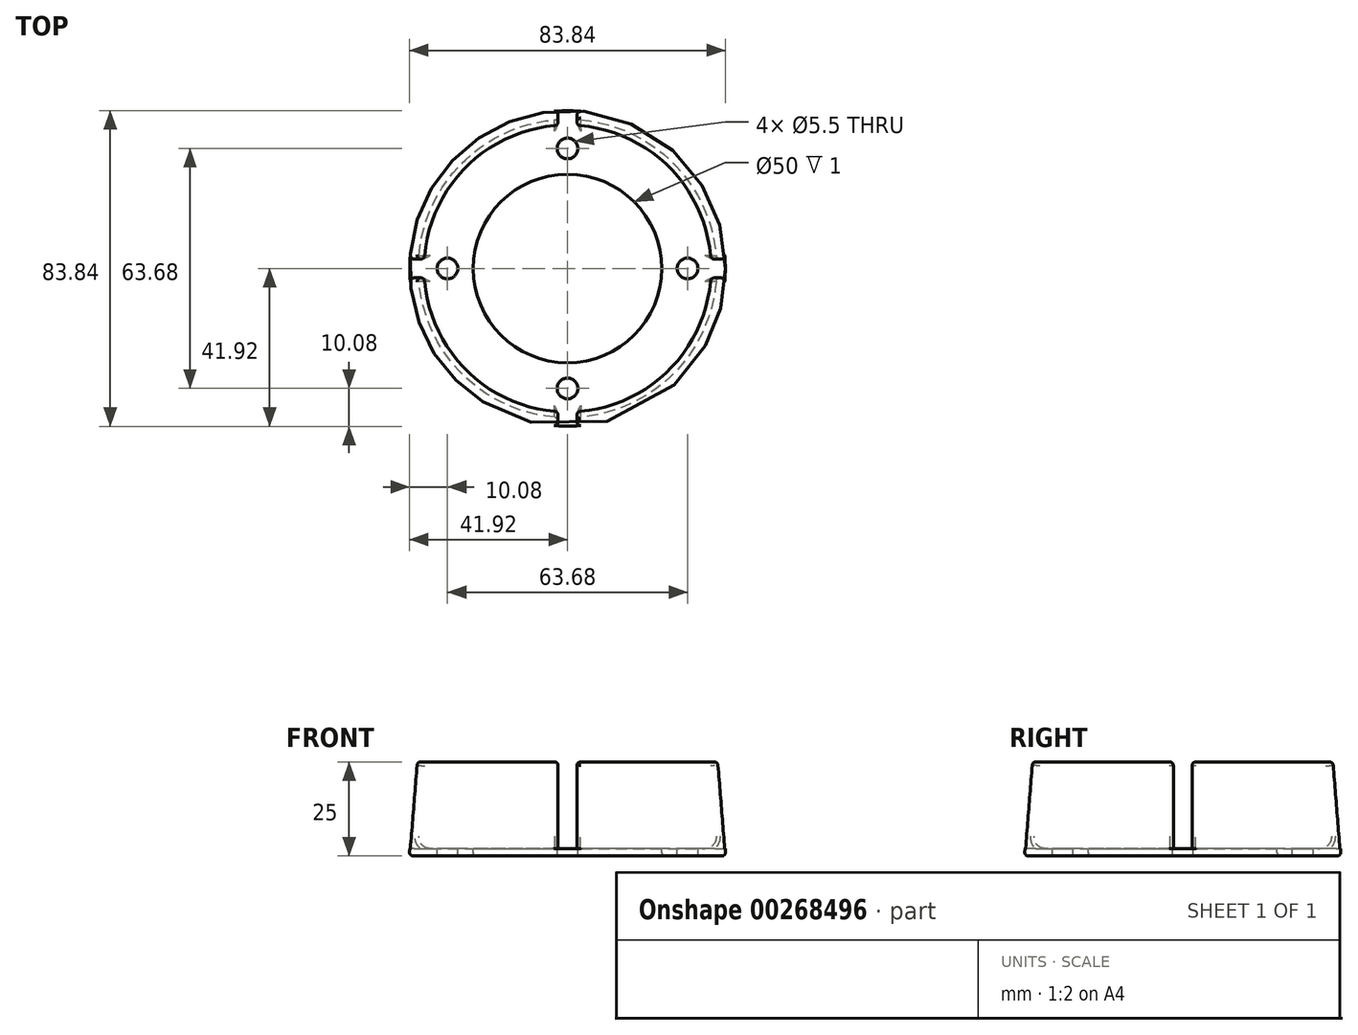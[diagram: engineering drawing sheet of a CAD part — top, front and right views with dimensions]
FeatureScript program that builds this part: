
annotation { "Feature Type Name" : "Feature", "Feature Type Description" : "" }
export const myFeature = defineFeature(function(context is Context, id is Id, definition is map)
    precondition{}
    {
        {
            var Q0;
            Q0=qCreatedBy(makeId("Top.planeOp"),FACE);
            var sketch = newSketch(context, id + "F0", { "sketchPlane" : qUnion([Q0])});
            skCircle(sketch, "E0", {"center": v(0, 0) * mm, "radius": 42 * mm});
            skSolve(sketch);
        }
        {
            var Q0;
            Q0=makeQuery(id+"F0.imprint","IMPRINT",FACE,{"disambiguationData":[TD([[makeQuery(id+"F0.imprint","IMPRINT",EDGE,{"derivedFrom":sQuery(id+"F0.wireOp",EDGE,"E0")}),1.0]])]});
            cPlane(context, id + "F1", {"entities" : qUnion([Q0]), "cplaneType" : CPlaneType.OFFSET, "offset" : 25 * mm, "width" : 150 * mm, "height" : 150 * mm});
        }
        {
            var Q0;
            Q0=qCreatedBy(id+"F1.planeOp",FACE);
            var sketch = newSketch(context, id + "F2", { "sketchPlane" : qUnion([Q0])});
            skCircle(sketch, "E1", {"center": v(0, 0) * mm, "radius": 40 * mm});
            skSolve(sketch);
        }
        {
            var Q0;
            Q0=makeQuery(id+"F0.imprint","IMPRINT",FACE,{"disambiguationData":[TD([[makeQuery(id+"F0.imprint","IMPRINT",EDGE,{"derivedFrom":sQuery(id+"F0.wireOp",EDGE,"E0")}),1.0]])]});
            var Q1;
            Q1=makeQuery(id+"F2.imprint","IMPRINT",FACE,{"disambiguationData":[TD([[makeQuery(id+"F2.imprint","IMPRINT",EDGE,{"derivedFrom":sQuery(id+"F2.wireOp",EDGE,"E1")}),1.0]])]});
            loft(context, id + "F3", {"sheetProfilesArray" : [{ "sheetProfileEntities" : qUnion([Q0]) }, { "sheetProfileEntities" : qUnion([Q1]) }]});
        }
        {
            var Q0;
            Q0=makeQuery(id+"F3.opLoft","CAP_FACE",FACE,{"disambiguationData":[OSD([makeQuery(id+"F2.imprint","IMPRINT",FACE,{"disambiguationData":[TD([[makeQuery(id+"F2.imprint","IMPRINT",EDGE,{"derivedFrom":sQuery(id+"F2.wireOp",EDGE,"E1")}),1.0]])]})])],"isStart":true});
            var Q1;
            Q1=makeQuery(id+"F3.opLoft","SWEPT_BODY",BODY,{"disambiguationData":[OSD([makeQuery(id+"F0.imprint","IMPRINT",FACE,{"disambiguationData":[TD([[makeQuery(id+"F0.imprint","IMPRINT",EDGE,{"derivedFrom":sQuery(id+"F0.wireOp",EDGE,"E0")}),1.0]])]}),makeQuery(id+"F2.imprint","IMPRINT",FACE,{"disambiguationData":[TD([[makeQuery(id+"F2.imprint","IMPRINT",EDGE,{"derivedFrom":sQuery(id+"F2.wireOp",EDGE,"E1")}),1.0]])]})])]});
            shell(context, id + "F4", {"entities" : qUnion([Q0]), "parts" : qUnion([Q1]), "thickness" : 2 * mm});
        }
        {
            var Q0;
            Q0=makeQuery(id+"F4.opShell","OFFSET_FACE",FACE,{"disambiguationData":[OSD([makeQuery(id+"F0.imprint","IMPRINT",FACE,{"disambiguationData":[TD([[makeQuery(id+"F0.imprint","IMPRINT",EDGE,{"derivedFrom":sQuery(id+"F0.wireOp",EDGE,"E0")}),1.0]])]})])]});
            var sketch = newSketch(context, id + "F5", { "sketchPlane" : qUnion([Q0])});
            skCircle(sketch, "E2", {"center": v(0, 0) * mm, "radius": 25 * mm});
            skSolve(sketch);
        }
        {
            var Q0;
            Q0=makeQuery(id+"F5.imprint","IMPRINT",FACE,{"disambiguationData":[TD([[makeQuery(id+"F5.imprint","IMPRINT",EDGE,{"derivedFrom":sQuery(id+"F5.wireOp",EDGE,"E2")}),1.0]])]});
            extrude(context, id + "F6", {"entities" : qUnion([Q0]), "operationType" : NewBodyOperationType.REMOVE, "oppositeDirection" : true, "depth" : 25 * mm});
        }
        {
            var Q0;
            Q0=qCreatedBy(id+"F1.planeOp",FACE);
            var sketch = newSketch(context, id + "F7", { "sketchPlane" : qUnion([Q0])});
            skLineSegment(sketch, "E3.bottom", {"start": v(-2.5, 65.52) * mm, "end": v(2.5, 65.52) * mm});
            skLineSegment(sketch, "E3.top", {"start": v(-2.5, -64.48) * mm, "end": v(2.5, -64.48) * mm});
            skLineSegment(sketch, "E3.left", {"start": v(-2.5, 65.52) * mm, "end": v(-2.5, -64.48) * mm});
            skLineSegment(sketch, "E3.right", {"start": v(2.5, 65.52) * mm, "end": v(2.5, -64.48) * mm});
            skLineSegment(sketch, "E4.bottom", {"start": v(-66.14, 2.5) * mm, "end": v(63.86, 2.5) * mm});
            skLineSegment(sketch, "E4.top", {"start": v(-66.14, -2.5) * mm, "end": v(63.86, -2.5) * mm});
            skLineSegment(sketch, "E4.left", {"start": v(-66.14, 2.5) * mm, "end": v(-66.14, -2.5) * mm});
            skLineSegment(sketch, "E4.right", {"start": v(63.86, 2.5) * mm, "end": v(63.86, -2.5) * mm});
            skSolve(sketch);
        }
        {
            var Q0;
            Q0 = qSketchRegion(id + "F7", true);
            extrude(context, id + "F8", {"entities" : qUnion([Q0]), "operationType" : NewBodyOperationType.REMOVE, "oppositeDirection" : true, "depth" : 23 * mm});
        }
        {
            var Q0;
            Q0=makeQuery(id+"F8.boolean.opBoolean","MERGE",FACE,{"derivedFrom":[makeQuery(id+"F4.opShell","OFFSET_FACE",FACE,{"disambiguationData":[OSD([makeQuery(id+"F0.imprint","IMPRINT",FACE,{"disambiguationData":[TD([[makeQuery(id+"F0.imprint","IMPRINT",EDGE,{"derivedFrom":sQuery(id+"F0.wireOp",EDGE,"E0")}),1.0]])]})])]}),makeQuery(id+"F8.opExtrude","CAP_FACE",FACE,{"disambiguationData":[OSD([sQuery(id+"F7.wireOp",EDGE,"E3.bottom"),sQuery(id+"F7.wireOp",EDGE,"E3.top"),sQuery(id+"F7.wireOp",EDGE,"E3.left"),sQuery(id+"F7.wireOp",EDGE,"E3.right"),sQuery(id+"F7.wireOp",EDGE,"E4.bottom"),sQuery(id+"F7.wireOp",EDGE,"E4.top"),sQuery(id+"F7.wireOp",EDGE,"E4.left"),sQuery(id+"F7.wireOp",EDGE,"E4.right")])],"isStart":false})]});
            var sketch = newSketch(context, id + "F9", { "sketchPlane" : qUnion([Q0])});
            skPoint(sketch, "E5", {"position": v(0, 31.84) * mm});
            skPoint(sketch, "E6.MirrorP", {"position": v(0, -31.84) * mm});
            skPoint(sketch, "E7", {"position": v(31.84, 0) * mm});
            skPoint(sketch, "E8.MirrorP", {"position": v(-31.84, 0) * mm});
            skSolve(sketch);
        }
        {
            var Q0;
            Q0=sQuery(id+"F9.wireOp",VERTEX,"E5");
            var Q1;
            Q1=sQuery(id+"F9.wireOp",VERTEX,"E8.MirrorP");
            var Q2;
            Q2=sQuery(id+"F9.wireOp",VERTEX,"E6.MirrorP");
            var Q3;
            Q3=sQuery(id+"F9.wireOp",VERTEX,"E7");
            var Q4;
            Q4=makeQuery(id+"F3.opLoft","SWEPT_BODY",BODY,{"disambiguationData":[OSD([makeQuery(id+"F0.imprint","IMPRINT",FACE,{"disambiguationData":[TD([[makeQuery(id+"F0.imprint","IMPRINT",EDGE,{"derivedFrom":sQuery(id+"F0.wireOp",EDGE,"E0")}),1.0]])]}),makeQuery(id+"F2.imprint","IMPRINT",FACE,{"disambiguationData":[TD([[makeQuery(id+"F2.imprint","IMPRINT",EDGE,{"derivedFrom":sQuery(id+"F2.wireOp",EDGE,"E1")}),1.0]])]})])]});
            hole(context, id + "F10", {"style" : HoleStyle.SIMPLE, "endStyle" : HoleEndStyle.BLIND, "standardTappedOrClearance" : lookupTablePath({ "standard" : "ISO", "fit" : "Normal", "size" : "M5", "type" : "Clearance" }), "standardBlindInLast" : lookupTablePath({ "fit" : "Standard", "standard" : "ISO", "size" : "M5", "type" : "Clearance" }), "holeDiameter" : 5.5 * mm, "holeDepth" : 50 * mm, "tappedDepth" : 12 * mm, "tapClearance" : 3, "locations" : qUnion([Q0, Q1, Q2, Q3]), "scope" : qUnion([Q4])});
        }
        {
            var Q0;
            {var subQ2=sQuery(id+"F7.wireOp",EDGE,"E3.left");var subQ3=sQuery(id+"F7.wireOp",EDGE,"E3.bottom");var subQ5=sQuery(id+"F0.wireOp",EDGE,"E0");Q0=makeQuery(id+"F8.boolean.opBoolean","SPLIT",EDGE,{"disambiguationData":[TD([makeQuery(id+"F8.opExtrude","SWEPT_FACE",FACE,{"disambiguationData":[OSD([subQ2]),TDD([makeQuery(id+"F7.imprint","IMPRINT",EDGE,{"disambiguationData":[TD([[makeQuery(id+"F7.imprint","INTERSECT",VERTEX,{"derivedFrom":[subQ3,subQ2]}),-1.0]])],"derivedFrom":subQ2})])]})])],"derivedFrom":makeQuery(id+"F4.opShell","OFFSET_EDGE",EDGE,{"disambiguationData":[OSD([subQ5])]})});}
            var Q1;
            {var subQ0=sQuery(id+"F7.wireOp",EDGE,"E3.right");var subQ1=sQuery(id+"F7.wireOp",EDGE,"E3.bottom");var subQ4=sQuery(id+"F0.wireOp",EDGE,"E0");Q1=makeQuery(id+"F8.boolean.opBoolean","SPLIT",EDGE,{"disambiguationData":[TD([makeQuery(id+"F8.opExtrude","SWEPT_FACE",FACE,{"disambiguationData":[OSD([subQ0]),TDD([makeQuery(id+"F7.imprint","IMPRINT",EDGE,{"disambiguationData":[TD([[makeQuery(id+"F7.imprint","INTERSECT",VERTEX,{"derivedFrom":[subQ1,subQ0]}),-1.0]])],"derivedFrom":subQ0})])]})])],"derivedFrom":makeQuery(id+"F4.opShell","OFFSET_EDGE",EDGE,{"disambiguationData":[OSD([subQ4])]})});}
            var Q2;
            {var subQ0=sQuery(id+"F7.wireOp",EDGE,"E3.left");var subQ1=sQuery(id+"F7.wireOp",EDGE,"E3.top");var subQ5=sQuery(id+"F0.wireOp",EDGE,"E0");Q2=makeQuery(id+"F8.boolean.opBoolean","SPLIT",EDGE,{"disambiguationData":[TD([makeQuery(id+"F8.opExtrude","SWEPT_FACE",FACE,{"disambiguationData":[OSD([subQ0]),TDD([makeQuery(id+"F7.imprint","IMPRINT",EDGE,{"disambiguationData":[TD([[makeQuery(id+"F7.imprint","INTERSECT",VERTEX,{"derivedFrom":[subQ1,subQ0]}),1.0]])],"derivedFrom":subQ0})])]})])],"derivedFrom":makeQuery(id+"F4.opShell","OFFSET_EDGE",EDGE,{"disambiguationData":[OSD([subQ5])]})});}
            var Q3;
            {var subQ0=sQuery(id+"F7.wireOp",EDGE,"E3.right");var subQ1=sQuery(id+"F7.wireOp",EDGE,"E3.top");var subQ5=sQuery(id+"F0.wireOp",EDGE,"E0");Q3=makeQuery(id+"F8.boolean.opBoolean","SPLIT",EDGE,{"disambiguationData":[TD([makeQuery(id+"F8.opExtrude","SWEPT_FACE",FACE,{"disambiguationData":[OSD([subQ0]),TDD([makeQuery(id+"F7.imprint","IMPRINT",EDGE,{"disambiguationData":[TD([[makeQuery(id+"F7.imprint","INTERSECT",VERTEX,{"derivedFrom":[subQ1,subQ0]}),1.0]])],"derivedFrom":subQ0})])]})])],"derivedFrom":makeQuery(id+"F4.opShell","OFFSET_EDGE",EDGE,{"disambiguationData":[OSD([subQ5])]})});}
            fillet(context, id + "F11", {"entities" : qUnion([Q0, Q1, Q2, Q3]), "radius" : 3 * mm, "tangentPropagation" : true, "allowEdgeOverflow" : false});
        }
        {
            var Q0;
            {var subQ0=sQuery(id+"F2.wireOp",EDGE,"E1");var subQ2=sQuery(id+"F7.wireOp",EDGE,"E3.left");Q0=makeQuery(id+"F8.boolean.opBoolean","SPLIT",FACE,{"disambiguationData":[TD([makeQuery(id+"F8.opExtrude","SWEPT_FACE",FACE,{"disambiguationData":[OSD([subQ2]),TDD([makeQuery(id+"F7.imprint","IMPRINT",EDGE,{"disambiguationData":[TD([[makeQuery(id+"F7.imprint","INTERSECT",VERTEX,{"derivedFrom":[sQuery(id+"F7.wireOp",EDGE,"E3.bottom"),subQ2]}),-1.0]])],"derivedFrom":subQ2})])]})])],"derivedFrom":makeQuery(id+"F3.opLoft","CAP_FACE",FACE,{"disambiguationData":[OSD([makeQuery(id+"F2.imprint","IMPRINT",FACE,{"disambiguationData":[TD([[makeQuery(id+"F2.imprint","IMPRINT",EDGE,{"derivedFrom":subQ0}),1.0]])]})])],"isStart":true})});}
            var Q1;
            {var subQ0=sQuery(id+"F2.wireOp",EDGE,"E1");var subQ3=sQuery(id+"F7.wireOp",EDGE,"E3.left");Q1=makeQuery(id+"F8.boolean.opBoolean","SPLIT",FACE,{"disambiguationData":[TD([makeQuery(id+"F8.opExtrude","SWEPT_FACE",FACE,{"disambiguationData":[OSD([subQ3]),TDD([makeQuery(id+"F7.imprint","IMPRINT",EDGE,{"disambiguationData":[TD([[makeQuery(id+"F7.imprint","INTERSECT",VERTEX,{"derivedFrom":[sQuery(id+"F7.wireOp",EDGE,"E3.top"),subQ3]}),1.0]])],"derivedFrom":subQ3})])]})])],"derivedFrom":makeQuery(id+"F3.opLoft","CAP_FACE",FACE,{"disambiguationData":[OSD([makeQuery(id+"F2.imprint","IMPRINT",FACE,{"disambiguationData":[TD([[makeQuery(id+"F2.imprint","IMPRINT",EDGE,{"derivedFrom":subQ0}),1.0]])]})])],"isStart":true})});}
            var Q2;
            {var subQ0=sQuery(id+"F2.wireOp",EDGE,"E1");var subQ3=sQuery(id+"F7.wireOp",EDGE,"E3.right");Q2=makeQuery(id+"F8.boolean.opBoolean","SPLIT",FACE,{"disambiguationData":[TD([makeQuery(id+"F8.opExtrude","SWEPT_FACE",FACE,{"disambiguationData":[OSD([subQ3]),TDD([makeQuery(id+"F7.imprint","IMPRINT",EDGE,{"disambiguationData":[TD([[makeQuery(id+"F7.imprint","INTERSECT",VERTEX,{"derivedFrom":[sQuery(id+"F7.wireOp",EDGE,"E3.bottom"),subQ3]}),-1.0]])],"derivedFrom":subQ3})])]})])],"derivedFrom":makeQuery(id+"F3.opLoft","CAP_FACE",FACE,{"disambiguationData":[OSD([makeQuery(id+"F2.imprint","IMPRINT",FACE,{"disambiguationData":[TD([[makeQuery(id+"F2.imprint","IMPRINT",EDGE,{"derivedFrom":subQ0}),1.0]])]})])],"isStart":true})});}
            var Q3;
            {var subQ0=sQuery(id+"F2.wireOp",EDGE,"E1");var subQ2=sQuery(id+"F7.wireOp",EDGE,"E3.right");Q3=makeQuery(id+"F8.boolean.opBoolean","SPLIT",FACE,{"disambiguationData":[TD([makeQuery(id+"F8.opExtrude","SWEPT_FACE",FACE,{"disambiguationData":[OSD([subQ2]),TDD([makeQuery(id+"F7.imprint","IMPRINT",EDGE,{"disambiguationData":[TD([[makeQuery(id+"F7.imprint","INTERSECT",VERTEX,{"derivedFrom":[sQuery(id+"F7.wireOp",EDGE,"E3.top"),subQ2]}),1.0]])],"derivedFrom":subQ2})])]})])],"derivedFrom":makeQuery(id+"F3.opLoft","CAP_FACE",FACE,{"disambiguationData":[OSD([makeQuery(id+"F2.imprint","IMPRINT",FACE,{"disambiguationData":[TD([[makeQuery(id+"F2.imprint","IMPRINT",EDGE,{"derivedFrom":subQ0}),1.0]])]})])],"isStart":true})});}
            fillet(context, id + "F12", {"entities" : qUnion([Q0, Q1, Q2, Q3]), "radius" : 1 * mm, "tangentPropagation" : true, "allowEdgeOverflow" : false});
        }
        {
            var Q0;
            Q0=makeQuery(id+"F6.boolean.opBoolean","INTERSECT",EDGE,{"derivedFrom":[makeQuery(id+"F3.opLoft","CAP_FACE",FACE,{"disambiguationData":[OSD([makeQuery(id+"F0.imprint","IMPRINT",FACE,{"disambiguationData":[TD([[makeQuery(id+"F0.imprint","IMPRINT",EDGE,{"derivedFrom":sQuery(id+"F0.wireOp",EDGE,"E0")}),1.0]])]})])],"isStart":true}),makeQuery(id+"F6.opExtrude","SWEPT_FACE",FACE,{"disambiguationData":[OSD([sQuery(id+"F5.wireOp",EDGE,"E2")])]})]});
            var Q1;
            Q1=makeQuery(id+"F6.boolean.opBoolean","COPY",EDGE,{"derivedFrom":makeQuery(id+"F6.opExtrude","CAP_EDGE",EDGE,{"disambiguationData":[OSD([sQuery(id+"F5.wireOp",EDGE,"E2")])],"isStart":true})});
            var Q2;
            Q2=makeQuery(id+"F10.hole-0.boolean.opBoolean","COPY",EDGE,{"derivedFrom":makeQuery(id+"F10.hole-0.opRevolve","SWEPT_EDGE",EDGE,{"disambiguationData":[OSD([sQuery(id+"F10.hole-0.sketch.wireOp",EDGE,"core_line_2"),sQuery(id+"F10.hole-0.sketch.wireOp",EDGE,"core_line_3")])]})});
            var Q3;
            Q3=makeQuery(id+"F10.hole-0.boolean.opBoolean","INTERSECT",EDGE,{"derivedFrom":[makeQuery(id+"F3.opLoft","CAP_FACE",FACE,{"disambiguationData":[OSD([makeQuery(id+"F0.imprint","IMPRINT",FACE,{"disambiguationData":[TD([[makeQuery(id+"F0.imprint","IMPRINT",EDGE,{"derivedFrom":sQuery(id+"F0.wireOp",EDGE,"E0")}),1.0]])]})])],"isStart":true}),makeQuery(id+"F10.hole-0.opRevolve","SWEPT_FACE",FACE,{"disambiguationData":[OSD([sQuery(id+"F10.hole-0.sketch.wireOp",EDGE,"core_line_2")])]})]});
            var Q4;
            Q4=makeQuery(id+"F10.hole-1.boolean.opBoolean","COPY",EDGE,{"derivedFrom":makeQuery(id+"F10.hole-1.opRevolve","SWEPT_EDGE",EDGE,{"disambiguationData":[OSD([sQuery(id+"F10.hole-1.sketch.wireOp",EDGE,"core_line_2"),sQuery(id+"F10.hole-1.sketch.wireOp",EDGE,"core_line_3")])]})});
            var Q5;
            Q5=makeQuery(id+"F10.hole-1.boolean.opBoolean","INTERSECT",EDGE,{"derivedFrom":[makeQuery(id+"F3.opLoft","CAP_FACE",FACE,{"disambiguationData":[OSD([makeQuery(id+"F0.imprint","IMPRINT",FACE,{"disambiguationData":[TD([[makeQuery(id+"F0.imprint","IMPRINT",EDGE,{"derivedFrom":sQuery(id+"F0.wireOp",EDGE,"E0")}),1.0]])]})])],"isStart":true}),makeQuery(id+"F10.hole-1.opRevolve","SWEPT_FACE",FACE,{"disambiguationData":[OSD([sQuery(id+"F10.hole-1.sketch.wireOp",EDGE,"core_line_2")])]})]});
            var Q6;
            Q6=makeQuery(id+"F10.hole-3.boolean.opBoolean","INTERSECT",EDGE,{"derivedFrom":[makeQuery(id+"F3.opLoft","CAP_FACE",FACE,{"disambiguationData":[OSD([makeQuery(id+"F0.imprint","IMPRINT",FACE,{"disambiguationData":[TD([[makeQuery(id+"F0.imprint","IMPRINT",EDGE,{"derivedFrom":sQuery(id+"F0.wireOp",EDGE,"E0")}),1.0]])]})])],"isStart":true}),makeQuery(id+"F10.hole-3.opRevolve","SWEPT_FACE",FACE,{"disambiguationData":[OSD([sQuery(id+"F10.hole-3.sketch.wireOp",EDGE,"core_line_2")])]})]});
            var Q7;
            Q7=makeQuery(id+"F10.hole-2.boolean.opBoolean","COPY",EDGE,{"derivedFrom":makeQuery(id+"F10.hole-2.opRevolve","SWEPT_EDGE",EDGE,{"disambiguationData":[OSD([sQuery(id+"F10.hole-2.sketch.wireOp",EDGE,"core_line_2"),sQuery(id+"F10.hole-2.sketch.wireOp",EDGE,"core_line_3")])]})});
            var Q8;
            Q8=makeQuery(id+"F10.hole-2.boolean.opBoolean","INTERSECT",EDGE,{"derivedFrom":[makeQuery(id+"F3.opLoft","CAP_FACE",FACE,{"disambiguationData":[OSD([makeQuery(id+"F0.imprint","IMPRINT",FACE,{"disambiguationData":[TD([[makeQuery(id+"F0.imprint","IMPRINT",EDGE,{"derivedFrom":sQuery(id+"F0.wireOp",EDGE,"E0")}),1.0]])]})])],"isStart":true}),makeQuery(id+"F10.hole-2.opRevolve","SWEPT_FACE",FACE,{"disambiguationData":[OSD([sQuery(id+"F10.hole-2.sketch.wireOp",EDGE,"core_line_2")])]})]});
            var Q9;
            Q9=makeQuery(id+"F10.hole-3.boolean.opBoolean","COPY",EDGE,{"derivedFrom":makeQuery(id+"F10.hole-3.opRevolve","SWEPT_EDGE",EDGE,{"disambiguationData":[OSD([sQuery(id+"F10.hole-3.sketch.wireOp",EDGE,"core_line_2"),sQuery(id+"F10.hole-3.sketch.wireOp",EDGE,"core_line_3")])]})});
            fillet(context, id + "F13", {"entities" : qUnion([Q0, Q1, Q2, Q3, Q4, Q5, Q6, Q7, Q8, Q9]), "radius" : 1 * mm, "tangentPropagation" : true, "allowEdgeOverflow" : false});
        }
        {
            var Q0;
            Q0=makeQuery(id+"F3.opLoft","MID_CAP_EDGE",EDGE,{"disambiguationData":[OSD([sQuery(id+"F0.wireOp",EDGE,"E0")])],"capPos":0.0});
            fillet(context, id + "F14", {"entities" : qUnion([Q0]), "radius" : 1 * mm, "tangentPropagation" : true, "allowEdgeOverflow" : false});
        }
        {
            var Q0;
            {var subQ0=sQuery(id+"F7.wireOp",EDGE,"E3.right");Q0=makeQuery(id+"F8.boolean.opBoolean","INTERSECT",EDGE,{"derivedFrom":[makeQuery(id+"F3.opLoft","SWEPT_FACE",FACE,{"disambiguationData":[OSD([sQuery(id+"F0.wireOp",EDGE,"E0"),sQuery(id+"F2.wireOp",EDGE,"E1")])]}),makeQuery(id+"F8.opExtrude","SWEPT_FACE",FACE,{"disambiguationData":[OSD([subQ0]),TDD([makeQuery(id+"F7.imprint","IMPRINT",EDGE,{"disambiguationData":[TD([[makeQuery(id+"F7.imprint","INTERSECT",VERTEX,{"derivedFrom":[sQuery(id+"F7.wireOp",EDGE,"E3.bottom"),subQ0]}),-1.0]])],"derivedFrom":subQ0})])]})]});}
            var Q1;
            {var subQ0=sQuery(id+"F7.wireOp",EDGE,"E3.right");Q1=makeQuery(id+"F8.boolean.opBoolean","INTERSECT",EDGE,{"derivedFrom":[makeQuery(id+"F4.opShell","OFFSET_FACE",FACE,{"disambiguationData":[OSD([sQuery(id+"F0.wireOp",EDGE,"E0"),sQuery(id+"F2.wireOp",EDGE,"E1")])]}),makeQuery(id+"F8.opExtrude","SWEPT_FACE",FACE,{"disambiguationData":[OSD([subQ0]),TDD([makeQuery(id+"F7.imprint","IMPRINT",EDGE,{"disambiguationData":[TD([[makeQuery(id+"F7.imprint","INTERSECT",VERTEX,{"derivedFrom":[sQuery(id+"F7.wireOp",EDGE,"E3.bottom"),subQ0]}),-1.0]])],"derivedFrom":subQ0})])]})]});}
            var Q2;
            {var subQ0=sQuery(id+"F7.wireOp",EDGE,"E3.right");var subQ1=sQuery(id+"F7.wireOp",EDGE,"E3.bottom");var subQ4=makeQuery(id+"F8.opExtrude","SWEPT_FACE",FACE,{"disambiguationData":[OSD([subQ0]),TDD([makeQuery(id+"F7.imprint","IMPRINT",EDGE,{"disambiguationData":[TD([[makeQuery(id+"F7.imprint","INTERSECT",VERTEX,{"derivedFrom":[subQ1,subQ0]}),-1.0]])],"derivedFrom":subQ0})])]});var subQ5=sQuery(id+"F0.wireOp",EDGE,"E0");Q2=makeQuery(id+"F11.opFillet","BLEND_EDGE",EDGE,{"blendedFrom":[makeQuery(id+"F8.boolean.opBoolean","SPLIT",EDGE,{"disambiguationData":[TD([subQ4])],"derivedFrom":makeQuery(id+"F4.opShell","OFFSET_EDGE",EDGE,{"disambiguationData":[OSD([subQ5])]})}),makeQuery(id+"F8.boolean.opBoolean","COPY",FACE,{"derivedFrom":subQ4})],"blendedInto":[makeQuery(id+"F8.boolean.opBoolean","COPY",FACE,{"derivedFrom":subQ4})]});}
            var Q3;
            {var subQ0=sQuery(id+"F7.wireOp",EDGE,"E4.bottom");Q3=makeQuery(id+"F8.boolean.opBoolean","INTERSECT",EDGE,{"derivedFrom":[makeQuery(id+"F4.opShell","OFFSET_FACE",FACE,{"disambiguationData":[OSD([sQuery(id+"F0.wireOp",EDGE,"E0"),sQuery(id+"F2.wireOp",EDGE,"E1")])]}),makeQuery(id+"F8.opExtrude","SWEPT_FACE",FACE,{"disambiguationData":[OSD([subQ0]),TDD([makeQuery(id+"F7.imprint","IMPRINT",EDGE,{"disambiguationData":[TD([[makeQuery(id+"F7.imprint","INTERSECT",VERTEX,{"derivedFrom":[subQ0,sQuery(id+"F7.wireOp",EDGE,"E4.right")]}),1.0]])],"derivedFrom":subQ0})])]})]});}
            var Q4;
            {var subQ0=sQuery(id+"F7.wireOp",EDGE,"E4.bottom");Q4=makeQuery(id+"F8.boolean.opBoolean","INTERSECT",EDGE,{"derivedFrom":[makeQuery(id+"F3.opLoft","SWEPT_FACE",FACE,{"disambiguationData":[OSD([sQuery(id+"F0.wireOp",EDGE,"E0"),sQuery(id+"F2.wireOp",EDGE,"E1")])]}),makeQuery(id+"F8.opExtrude","SWEPT_FACE",FACE,{"disambiguationData":[OSD([subQ0]),TDD([makeQuery(id+"F7.imprint","IMPRINT",EDGE,{"disambiguationData":[TD([[makeQuery(id+"F7.imprint","INTERSECT",VERTEX,{"derivedFrom":[subQ0,sQuery(id+"F7.wireOp",EDGE,"E4.right")]}),1.0]])],"derivedFrom":subQ0})])]})]});}
            var Q5;
            {var subQ0=sQuery(id+"F7.wireOp",EDGE,"E4.bottom");Q5=makeQuery(id+"F8.boolean.opBoolean","INTERSECT",EDGE,{"derivedFrom":[makeQuery(id+"F3.opLoft","SWEPT_FACE",FACE,{"disambiguationData":[OSD([sQuery(id+"F0.wireOp",EDGE,"E0"),sQuery(id+"F2.wireOp",EDGE,"E1")])]}),makeQuery(id+"F8.opExtrude","SWEPT_FACE",FACE,{"disambiguationData":[OSD([subQ0]),TDD([makeQuery(id+"F7.imprint","IMPRINT",EDGE,{"disambiguationData":[TD([[makeQuery(id+"F7.imprint","INTERSECT",VERTEX,{"derivedFrom":[subQ0,sQuery(id+"F7.wireOp",EDGE,"E4.left")]}),-1.0]])],"derivedFrom":subQ0})])]})]});}
            var Q6;
            {var subQ0=sQuery(id+"F7.wireOp",EDGE,"E4.bottom");Q6=makeQuery(id+"F8.boolean.opBoolean","INTERSECT",EDGE,{"derivedFrom":[makeQuery(id+"F4.opShell","OFFSET_FACE",FACE,{"disambiguationData":[OSD([sQuery(id+"F0.wireOp",EDGE,"E0"),sQuery(id+"F2.wireOp",EDGE,"E1")])]}),makeQuery(id+"F8.opExtrude","SWEPT_FACE",FACE,{"disambiguationData":[OSD([subQ0]),TDD([makeQuery(id+"F7.imprint","IMPRINT",EDGE,{"disambiguationData":[TD([[makeQuery(id+"F7.imprint","INTERSECT",VERTEX,{"derivedFrom":[subQ0,sQuery(id+"F7.wireOp",EDGE,"E4.left")]}),-1.0]])],"derivedFrom":subQ0})])]})]});}
            var Q7;
            {var subQ0=sQuery(id+"F7.wireOp",EDGE,"E4.top");Q7=makeQuery(id+"F8.boolean.opBoolean","INTERSECT",EDGE,{"derivedFrom":[makeQuery(id+"F3.opLoft","SWEPT_FACE",FACE,{"disambiguationData":[OSD([sQuery(id+"F0.wireOp",EDGE,"E0"),sQuery(id+"F2.wireOp",EDGE,"E1")])]}),makeQuery(id+"F8.opExtrude","SWEPT_FACE",FACE,{"disambiguationData":[OSD([subQ0]),TDD([makeQuery(id+"F7.imprint","IMPRINT",EDGE,{"disambiguationData":[TD([[makeQuery(id+"F7.imprint","INTERSECT",VERTEX,{"derivedFrom":[subQ0,sQuery(id+"F7.wireOp",EDGE,"E4.left")]}),-1.0]])],"derivedFrom":subQ0})])]})]});}
            var Q8;
            {var subQ0=sQuery(id+"F7.wireOp",EDGE,"E3.left");Q8=makeQuery(id+"F8.boolean.opBoolean","INTERSECT",EDGE,{"derivedFrom":[makeQuery(id+"F4.opShell","OFFSET_FACE",FACE,{"disambiguationData":[OSD([sQuery(id+"F0.wireOp",EDGE,"E0"),sQuery(id+"F2.wireOp",EDGE,"E1")])]}),makeQuery(id+"F8.opExtrude","SWEPT_FACE",FACE,{"disambiguationData":[OSD([subQ0]),TDD([makeQuery(id+"F7.imprint","IMPRINT",EDGE,{"disambiguationData":[TD([[makeQuery(id+"F7.imprint","INTERSECT",VERTEX,{"derivedFrom":[sQuery(id+"F7.wireOp",EDGE,"E3.bottom"),subQ0]}),-1.0]])],"derivedFrom":subQ0})])]})]});}
            var Q9;
            {var subQ0=sQuery(id+"F7.wireOp",EDGE,"E4.top");Q9=makeQuery(id+"F8.boolean.opBoolean","INTERSECT",EDGE,{"derivedFrom":[makeQuery(id+"F4.opShell","OFFSET_FACE",FACE,{"disambiguationData":[OSD([sQuery(id+"F0.wireOp",EDGE,"E0"),sQuery(id+"F2.wireOp",EDGE,"E1")])]}),makeQuery(id+"F8.opExtrude","SWEPT_FACE",FACE,{"disambiguationData":[OSD([subQ0]),TDD([makeQuery(id+"F7.imprint","IMPRINT",EDGE,{"disambiguationData":[TD([[makeQuery(id+"F7.imprint","INTERSECT",VERTEX,{"derivedFrom":[subQ0,sQuery(id+"F7.wireOp",EDGE,"E4.right")]}),1.0]])],"derivedFrom":subQ0})])]})]});}
            var Q10;
            {var subQ0=sQuery(id+"F7.wireOp",EDGE,"E3.right");Q10=makeQuery(id+"F8.boolean.opBoolean","INTERSECT",EDGE,{"derivedFrom":[makeQuery(id+"F4.opShell","OFFSET_FACE",FACE,{"disambiguationData":[OSD([sQuery(id+"F0.wireOp",EDGE,"E0"),sQuery(id+"F2.wireOp",EDGE,"E1")])]}),makeQuery(id+"F8.opExtrude","SWEPT_FACE",FACE,{"disambiguationData":[OSD([subQ0]),TDD([makeQuery(id+"F7.imprint","IMPRINT",EDGE,{"disambiguationData":[TD([[makeQuery(id+"F7.imprint","INTERSECT",VERTEX,{"derivedFrom":[sQuery(id+"F7.wireOp",EDGE,"E3.top"),subQ0]}),1.0]])],"derivedFrom":subQ0})])]})]});}
            var Q11;
            {var subQ0=sQuery(id+"F7.wireOp",EDGE,"E3.right");Q11=makeQuery(id+"F8.boolean.opBoolean","INTERSECT",EDGE,{"derivedFrom":[makeQuery(id+"F3.opLoft","SWEPT_FACE",FACE,{"disambiguationData":[OSD([sQuery(id+"F0.wireOp",EDGE,"E0"),sQuery(id+"F2.wireOp",EDGE,"E1")])]}),makeQuery(id+"F8.opExtrude","SWEPT_FACE",FACE,{"disambiguationData":[OSD([subQ0]),TDD([makeQuery(id+"F7.imprint","IMPRINT",EDGE,{"disambiguationData":[TD([[makeQuery(id+"F7.imprint","INTERSECT",VERTEX,{"derivedFrom":[sQuery(id+"F7.wireOp",EDGE,"E3.top"),subQ0]}),1.0]])],"derivedFrom":subQ0})])]})]});}
            var Q12;
            {var subQ0=sQuery(id+"F7.wireOp",EDGE,"E3.left");Q12=makeQuery(id+"F8.boolean.opBoolean","INTERSECT",EDGE,{"derivedFrom":[makeQuery(id+"F3.opLoft","SWEPT_FACE",FACE,{"disambiguationData":[OSD([sQuery(id+"F0.wireOp",EDGE,"E0"),sQuery(id+"F2.wireOp",EDGE,"E1")])]}),makeQuery(id+"F8.opExtrude","SWEPT_FACE",FACE,{"disambiguationData":[OSD([subQ0]),TDD([makeQuery(id+"F7.imprint","IMPRINT",EDGE,{"disambiguationData":[TD([[makeQuery(id+"F7.imprint","INTERSECT",VERTEX,{"derivedFrom":[sQuery(id+"F7.wireOp",EDGE,"E3.top"),subQ0]}),1.0]])],"derivedFrom":subQ0})])]})]});}
            var Q13;
            {var subQ0=sQuery(id+"F7.wireOp",EDGE,"E4.top");Q13=makeQuery(id+"F8.boolean.opBoolean","INTERSECT",EDGE,{"derivedFrom":[makeQuery(id+"F3.opLoft","SWEPT_FACE",FACE,{"disambiguationData":[OSD([sQuery(id+"F0.wireOp",EDGE,"E0"),sQuery(id+"F2.wireOp",EDGE,"E1")])]}),makeQuery(id+"F8.opExtrude","SWEPT_FACE",FACE,{"disambiguationData":[OSD([subQ0]),TDD([makeQuery(id+"F7.imprint","IMPRINT",EDGE,{"disambiguationData":[TD([[makeQuery(id+"F7.imprint","INTERSECT",VERTEX,{"derivedFrom":[subQ0,sQuery(id+"F7.wireOp",EDGE,"E4.right")]}),1.0]])],"derivedFrom":subQ0})])]})]});}
            var Q14;
            {var subQ0=sQuery(id+"F7.wireOp",EDGE,"E3.left");Q14=makeQuery(id+"F8.boolean.opBoolean","INTERSECT",EDGE,{"derivedFrom":[makeQuery(id+"F3.opLoft","SWEPT_FACE",FACE,{"disambiguationData":[OSD([sQuery(id+"F0.wireOp",EDGE,"E0"),sQuery(id+"F2.wireOp",EDGE,"E1")])]}),makeQuery(id+"F8.opExtrude","SWEPT_FACE",FACE,{"disambiguationData":[OSD([subQ0]),TDD([makeQuery(id+"F7.imprint","IMPRINT",EDGE,{"disambiguationData":[TD([[makeQuery(id+"F7.imprint","INTERSECT",VERTEX,{"derivedFrom":[sQuery(id+"F7.wireOp",EDGE,"E3.bottom"),subQ0]}),-1.0]])],"derivedFrom":subQ0})])]})]});}
            var Q15;
            {var subQ0=sQuery(id+"F7.wireOp",EDGE,"E3.left");Q15=makeQuery(id+"F8.boolean.opBoolean","INTERSECT",EDGE,{"derivedFrom":[makeQuery(id+"F4.opShell","OFFSET_FACE",FACE,{"disambiguationData":[OSD([sQuery(id+"F0.wireOp",EDGE,"E0"),sQuery(id+"F2.wireOp",EDGE,"E1")])]}),makeQuery(id+"F8.opExtrude","SWEPT_FACE",FACE,{"disambiguationData":[OSD([subQ0]),TDD([makeQuery(id+"F7.imprint","IMPRINT",EDGE,{"disambiguationData":[TD([[makeQuery(id+"F7.imprint","INTERSECT",VERTEX,{"derivedFrom":[sQuery(id+"F7.wireOp",EDGE,"E3.top"),subQ0]}),1.0]])],"derivedFrom":subQ0})])]})]});}
            var Q16;
            {var subQ0=sQuery(id+"F7.wireOp",EDGE,"E4.top");Q16=makeQuery(id+"F8.boolean.opBoolean","INTERSECT",EDGE,{"derivedFrom":[makeQuery(id+"F4.opShell","OFFSET_FACE",FACE,{"disambiguationData":[OSD([sQuery(id+"F0.wireOp",EDGE,"E0"),sQuery(id+"F2.wireOp",EDGE,"E1")])]}),makeQuery(id+"F8.opExtrude","SWEPT_FACE",FACE,{"disambiguationData":[OSD([subQ0]),TDD([makeQuery(id+"F7.imprint","IMPRINT",EDGE,{"disambiguationData":[TD([[makeQuery(id+"F7.imprint","INTERSECT",VERTEX,{"derivedFrom":[subQ0,sQuery(id+"F7.wireOp",EDGE,"E4.left")]}),-1.0]])],"derivedFrom":subQ0})])]})]});}
            fillet(context, id + "F15", {"entities" : qUnion([Q0, Q1, Q2, Q3, Q4, Q5, Q6, Q7, Q8, Q9, Q10, Q11, Q12, Q13, Q14, Q15, Q16]), "radius" : 1 * mm, "tangentPropagation" : true, "allowEdgeOverflow" : false});
        }
    });
